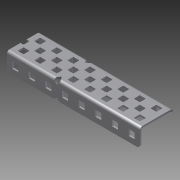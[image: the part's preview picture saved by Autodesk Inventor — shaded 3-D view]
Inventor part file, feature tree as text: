
AUTODESK INVENTOR PART (.ipt)
format: ipt  version: 2014 SP1 (Build 180222100, 222)  size: 631,296 bytes
history: native  units: in
note: dims shown in document units (in); Inventor stores cm internally (conversion verified against a paired STEP export)
features: other x3, sketch x2
ambient origin geometry x8: Origin, YZ Plane, XZ Plane, XY Plane, X Axis, Y Axis, Z Axis, Center Point
bodies: Solid1 (feature_tree)
feature tree (5):
  other  "2 x 8 holes for large ball knockers.ipt"
  other  "NONE::2 x 8 holes for large ball knockers.ipt"
  other  "TaggingFeature1"
  sketch  "Sketch2"  dims[d0=0.3937in]
  sketch  "Sketch4"  dims[d1=1.0in d2=0.0in d3=0.5in d4=1.0in d5=0.5in d7=0.0in]
